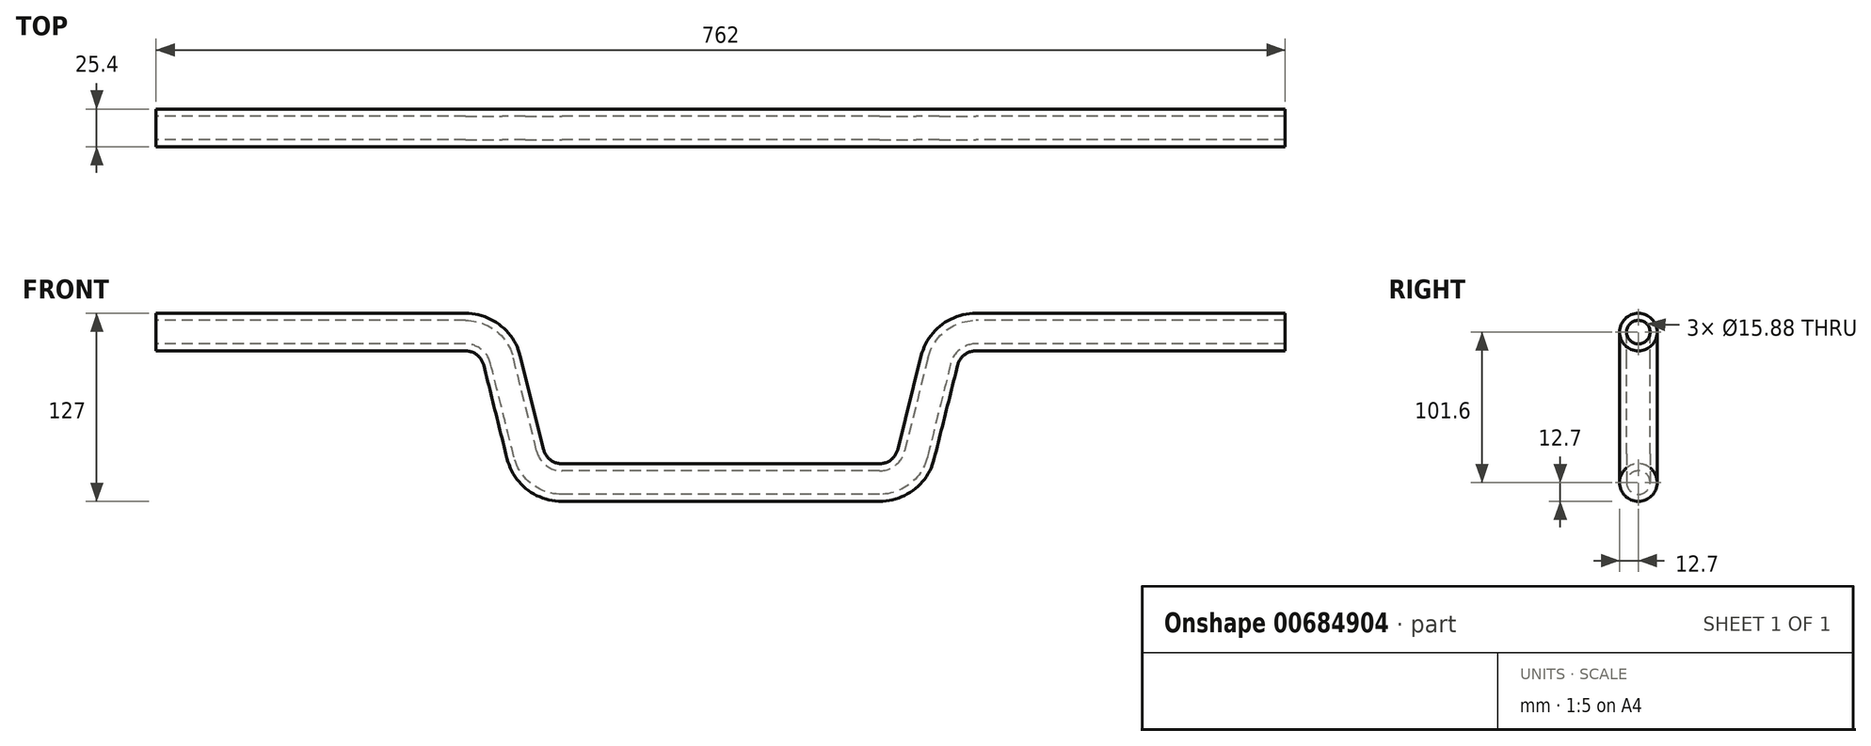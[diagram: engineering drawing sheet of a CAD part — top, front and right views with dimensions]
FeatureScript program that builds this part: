
annotation { "Feature Type Name" : "Feature", "Feature Type Description" : "" }
export const myFeature = defineFeature(function(context is Context, id is Id, definition is map)
    precondition{}
    {
        {
            var Q0;
            Q0=qCreatedBy(makeId("Front.planeOp"),FACE);
            var sketch = newSketch(context, id + "F0", { "sketchPlane" : qUnion([Q0])});
            skLineSegment(sketch, "E0", {"start": v(172.23, 0) * mm, "end": v(381, 0) * mm});
            skLineSegment(sketch, "E1", {"start": v(0, 299.62) * mm, "end": v(0, -392.92) * mm, "construction": true});
            skLineSegment(sketch, "E2", {"start": v(-101.06, 0) * mm, "end": v(111.4, 0) * mm, "construction": true});
            skLineSegment(sketch, "E3.MirrorCS", {"start": v(-172.23, 0) * mm, "end": v(-381, 0) * mm});
            skPoint(sketch, "E4.visualSharp", {"position": v(4518.56, 0) * mm});
            skPoint(sketch, "E5.orphan", {"position": v(-4518.56, 0) * mm});
            skLineSegment(sketch, "E6", {"start": v(-147.6, -19.24) * mm, "end": v(-131.8, -82.36) * mm});
            skLineSegment(sketch, "E7", {"start": v(-107.17, -101.6) * mm, "end": v(107.17, -101.6) * mm});
            skLineSegment(sketch, "E8.MirrorCS", {"start": v(147.6, -19.24) * mm, "end": v(131.8, -82.36) * mm});
            skPoint(sketch, "E9.visualSharp", {"position": v(-152.4, 0) * mm});
            skArc(sketch, "E9.filletArc", {"start": v(-147.6, -19.24) * mm, "mid": v(-156.6, -5.38) * mm, "end": v(-172.23, 0) * mm});
            skPoint(sketch, "E10.visualSharp", {"position": v(-127, -101.6) * mm});
            skArc(sketch, "E10.filletArc", {"start": v(-131.8, -82.36) * mm, "mid": v(-122.8, -96.22) * mm, "end": v(-107.17, -101.6) * mm});
            skPoint(sketch, "E11.visualSharp", {"position": v(127, -101.6) * mm});
            skArc(sketch, "E11.filletArc", {"start": v(107.17, -101.6) * mm, "mid": v(122.8, -96.22) * mm, "end": v(131.8, -82.36) * mm});
            skPoint(sketch, "E12.visualSharp", {"position": v(152.4, 0) * mm});
            skArc(sketch, "E12.filletArc", {"start": v(172.23, 0) * mm, "mid": v(156.6, -5.38) * mm, "end": v(147.6, -19.24) * mm});
            skSolve(sketch);
        }
        {
            var Q0;
            Q0=qCreatedBy(makeId("Right.planeOp"),FACE);
            cPlane(context, id + "F1", {"entities" : qUnion([Q0]), "cplaneType" : CPlaneType.OFFSET, "offset" : 381 * mm, "width" : 152.4 * mm, "height" : 152.4 * mm});
        }
        {
            var Q0;
            Q0=qCreatedBy(id+"F1.planeOp",FACE);
            var sketch = newSketch(context, id + "F2", { "sketchPlane" : qUnion([Q0])});
            skCircle(sketch, "E13", {"center": v(0, 0) * mm, "radius": 12.7 * mm});
            skCircle(sketch, "E14", {"center": v(0, 0) * mm, "radius": 7.94 * mm});
            skSolve(sketch);
        }
        {
            var Q0;
            Q0 = qSketchRegion(id + "F2", true);
            var Q1;
            Q1 = qConstructionFilter(qBodyType(qCreatedBy(id + "F0" ,EDGE), BodyType.WIRE), ConstructionObject.NO);
            sweep(context, id + "F3", {"profiles" : qUnion([Q0]), "path" : qUnion([Q1])});
        }
    });
